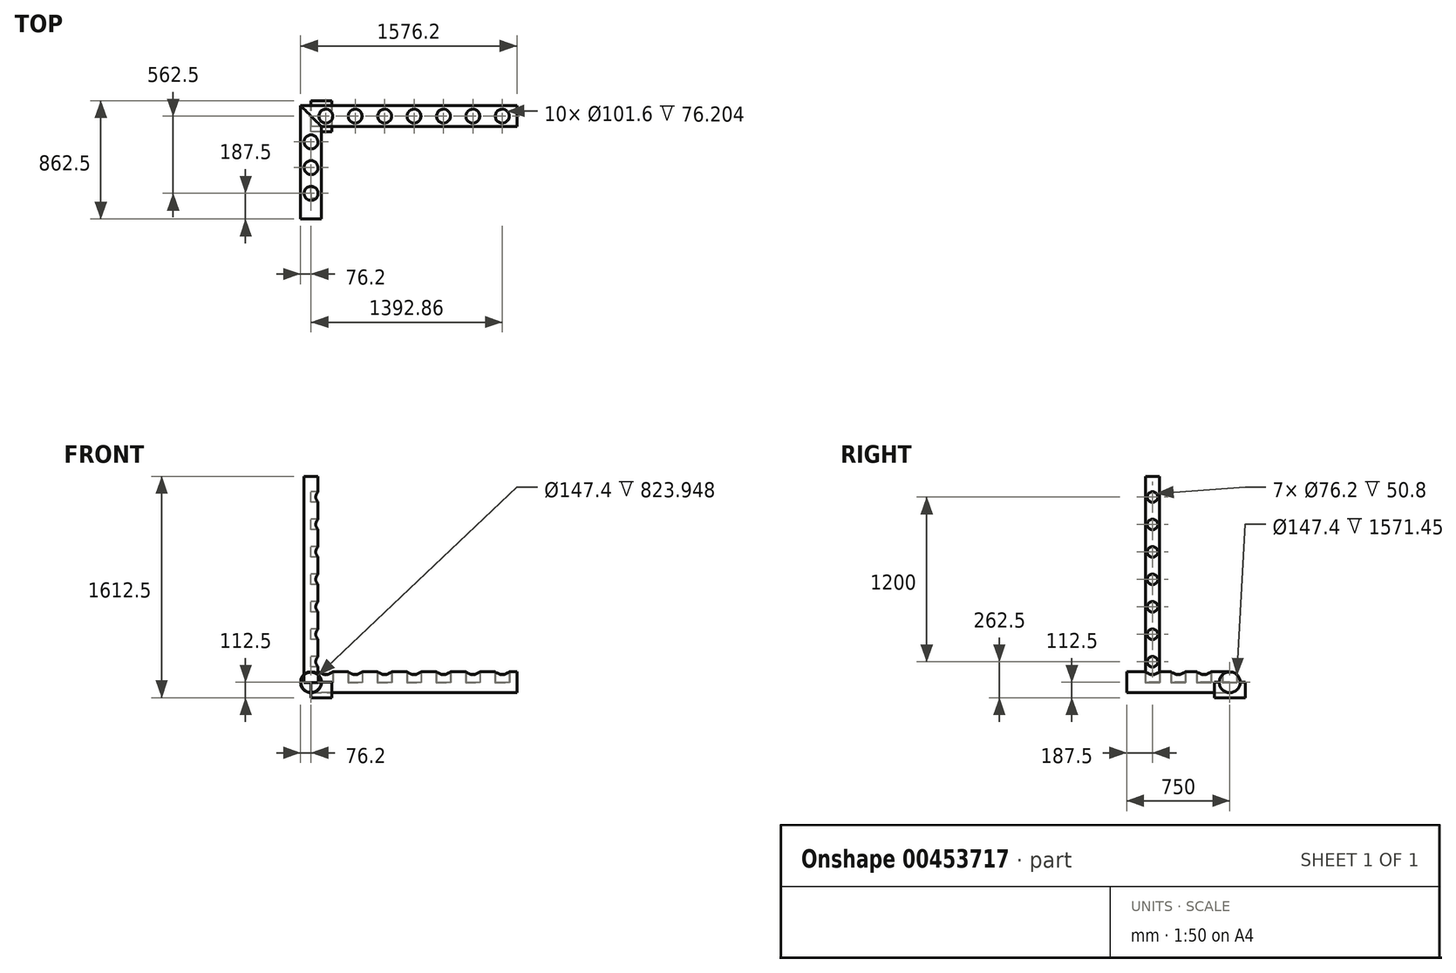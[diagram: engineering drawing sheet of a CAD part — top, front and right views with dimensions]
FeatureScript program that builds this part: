
annotation { "Feature Type Name" : "Feature", "Feature Type Description" : "" }
export const myFeature = defineFeature(function(context is Context, id is Id, definition is map)
    precondition{}
    {
        {
            var Q0;
            Q0=qCreatedBy(makeId("Top.planeOp"),FACE);
            var sketch = newSketch(context, id + "F0", { "sketchPlane" : qUnion([Q0])});
            skLineSegment(sketch, "E0", {"start": v(0, 0) * mm, "end": v(0, 750) * mm});
            skLineSegment(sketch, "E1", {"start": v(0, 750) * mm, "end": v(1500, 750) * mm});
            skPoint(sketch, "E2", {"position": v(0, 562.5) * mm});
            skPoint(sketch, "E3", {"position": v(0, 375) * mm});
            skPoint(sketch, "E4", {"position": v(0, 187.5) * mm});
            skPoint(sketch, "E5", {"position": v(750, 750) * mm});
            skPoint(sketch, "E6", {"position": v(535.71, 750) * mm});
            skPoint(sketch, "E7", {"position": v(964.29, 750) * mm});
            skPoint(sketch, "E8", {"position": v(321.43, 750) * mm});
            skPoint(sketch, "E9", {"position": v(1178.57, 750) * mm});
            skPoint(sketch, "E10", {"position": v(107.14, 750) * mm});
            skPoint(sketch, "E11", {"position": v(1392.86, 750) * mm});
            skSolve(sketch);
        }
        {
            var Q0;
            Q0=qCreatedBy(makeId("Front.planeOp"),FACE);
            var sketch = newSketch(context, id + "F1", { "sketchPlane" : qUnion([Q0])});
            skCircle(sketch, "E12", {"center": v(0, 0) * mm, "radius": 76.2 * mm});
            skSolve(sketch);
        }
        {
            var Q0;
            Q0=makeQuery(id+"F1.imprint","IMPRINT",FACE,{"disambiguationData":[TD([[makeQuery(id+"F1.imprint","IMPRINT",EDGE,{"derivedFrom":sQuery(id+"F1.wireOp",EDGE,"E12")}),1.0]])]});
            var Q1;
            Q1=sQuery(id+"F0.wireOp",EDGE,"E0");
            var Q2;
            Q2=sQuery(id+"F0.wireOp",EDGE,"E1");
            sweep(context, id + "F2", {"profiles" : qUnion([Q0]), "path" : qUnion([Q1, Q2])});
        }
        {
            var Q0;
            Q0=qCreatedBy(makeId("Top.planeOp"),FACE);
            var sketch = newSketch(context, id + "F3", { "sketchPlane" : qUnion([Q0])});
            skPoint(sketch, "E13.0", {"position": v(0, 187.5) * mm});
            skPoint(sketch, "E14.0", {"position": v(0, 375) * mm});
            skPoint(sketch, "E15.0", {"position": v(0, 562.5) * mm});
            skPoint(sketch, "E16.0", {"position": v(107.14, 750) * mm});
            skPoint(sketch, "E17.0", {"position": v(321.43, 750) * mm});
            skPoint(sketch, "E18.0", {"position": v(535.71, 750) * mm});
            skPoint(sketch, "E19.0", {"position": v(750, 750) * mm});
            skPoint(sketch, "E20.0", {"position": v(964.29, 750) * mm});
            skPoint(sketch, "E21.0", {"position": v(1178.57, 750) * mm});
            skPoint(sketch, "E22.0", {"position": v(1392.86, 750) * mm});
            skCircle(sketch, "E23", {"center": v(0, 187.5) * mm, "radius": 50.8 * mm});
            skCircle(sketch, "E24", {"center": v(0, 375) * mm, "radius": 50.8 * mm});
            skCircle(sketch, "E25", {"center": v(0, 562.5) * mm, "radius": 50.8 * mm});
            skCircle(sketch, "E26", {"center": v(107.14, 750) * mm, "radius": 50.8 * mm});
            skCircle(sketch, "E27", {"center": v(321.43, 750) * mm, "radius": 50.8 * mm});
            skCircle(sketch, "E28", {"center": v(535.71, 750) * mm, "radius": 50.8 * mm});
            skCircle(sketch, "E29", {"center": v(750, 750) * mm, "radius": 50.8 * mm});
            skCircle(sketch, "E30", {"center": v(964.29, 750) * mm, "radius": 50.8 * mm});
            skCircle(sketch, "E31", {"center": v(1178.57, 750) * mm, "radius": 50.8 * mm});
            skCircle(sketch, "E32", {"center": v(1392.86, 750) * mm, "radius": 50.8 * mm});
            skSolve(sketch);
        }
        {
            var Q0;
            Q0 = qSketchRegion(id + "F3", true);
            extrude(context, id + "F4", {"entities" : qUnion([Q0]), "operationType" : NewBodyOperationType.REMOVE, "endBound" : BoundingType.THROUGH_ALL, "depth" : 25 * mm});
        }
        {
            var Q0;
            Q0=makeQuery(id+"F2.opSweep","CAP_FACE",FACE,{"disambiguationData":[OSD([sQuery(id+"F0.wireOp",VERTEX,"E0.start"),sQuery(id+"F1.wireOp",EDGE,"E12")])],"isStart":true});
            shell(context, id + "F5", {"entities" : qUnion([Q0]), "thickness" : 2.5 * mm});
        }
        {
            var Q0;
            Q0=makeQuery(id+"F4.boolean.opBoolean","COPY",FACE,{"derivedFrom":makeQuery(id+"F4.opExtrude","CAP_FACE",FACE,{"disambiguationData":[OSD([sQuery(id+"F3.wireOp",EDGE,"E23")])],"isStart":true})});
            var sketch = newSketch(context, id + "F6", { "sketchPlane" : qUnion([Q0])});
            skCircle(sketch, "E33", {"center": v(0, 187.5) * mm, "radius": 50.8 * mm});
            skSolve(sketch);
        }
        {
            var Q0;
            Q0 = qSketchRegion(id + "F6", true);
            extrude(context, id + "F7", {"entities" : qUnion([Q0]), "depth" : 1500 * mm});
        }
        {
            var Q0;
            Q0=qCreatedBy(makeId("Right.planeOp"),FACE);
            var sketch = newSketch(context, id + "F8", { "sketchPlane" : qUnion([Q0])});
            skPoint(sketch, "E34.0", {"position": v(187.5, 0) * mm});
            skLineSegment(sketch, "E35", {"start": v(187.5, 0) * mm, "end": v(187.5, 1500) * mm, "construction": true});
            skLineSegment(sketch, "E36.0", {"start": v(136.7, 1500) * mm, "end": v(238.3, 1500) * mm, "construction": true});
            skCircle(sketch, "E37", {"center": v(187.5, 750) * mm, "radius": 38.1 * mm});
            skCircle(sketch, "E38", {"center": v(187.5, 950) * mm, "radius": 38.1 * mm});
            skCircle(sketch, "E39", {"center": v(187.5, 1150) * mm, "radius": 38.1 * mm});
            skCircle(sketch, "E40", {"center": v(187.5, 1350) * mm, "radius": 38.1 * mm});
            skCircle(sketch, "E41", {"center": v(187.5, 550) * mm, "radius": 38.1 * mm});
            skCircle(sketch, "E42", {"center": v(187.5, 350) * mm, "radius": 38.1 * mm});
            skCircle(sketch, "E43", {"center": v(187.5, 150) * mm, "radius": 38.1 * mm});
            skSolve(sketch);
        }
        {
            var Q0;
            Q0 = qSketchRegion(id + "F8", true);
            extrude(context, id + "F9", {"entities" : qUnion([Q0]), "operationType" : NewBodyOperationType.REMOVE, "endBound" : BoundingType.THROUGH_ALL, "depth" : 25 * mm});
        }
        {
            var Q0;
            Q0=qCreatedBy(makeId("Right.planeOp"),FACE);
            var sketch = newSketch(context, id + "F10", { "sketchPlane" : qUnion([Q0])});
            skPoint(sketch, "E44.0", {"position": v(750, 0) * mm});
            skLineSegment(sketch, "E45.bottom", {"start": v(862.5, -112.5) * mm, "end": v(637.5, -112.5) * mm});
            skLineSegment(sketch, "E45.left", {"start": v(862.5, -112.5) * mm, "end": v(862.5, 0) * mm});
            skLineSegment(sketch, "E45.right", {"start": v(637.5, -112.5) * mm, "end": v(637.5, 0) * mm});
            skArc(sketch, "E46.0", {"start": v(673.8, 0) * mm, "mid": v(750, -76.2) * mm, "end": v(826.2, 0) * mm});
            skLineSegment(sketch, "E47", {"start": v(637.5, 0) * mm, "end": v(673.8, 0) * mm});
            skLineSegment(sketch, "E48", {"start": v(862.5, 0) * mm, "end": v(826.2, 0) * mm});
            skPoint(sketch, "E49.orphan", {"position": v(862.5, 112.5) * mm});
            skPoint(sketch, "E50.orphan", {"position": v(637.5, 112.5) * mm});
            skSolve(sketch);
        }
        {
            var Q0;
            Q0 = qSketchRegion(id + "F10", true);
            extrude(context, id + "F11", {"entities" : qUnion([Q0]), "depth" : 150 * mm});
        }
    });
